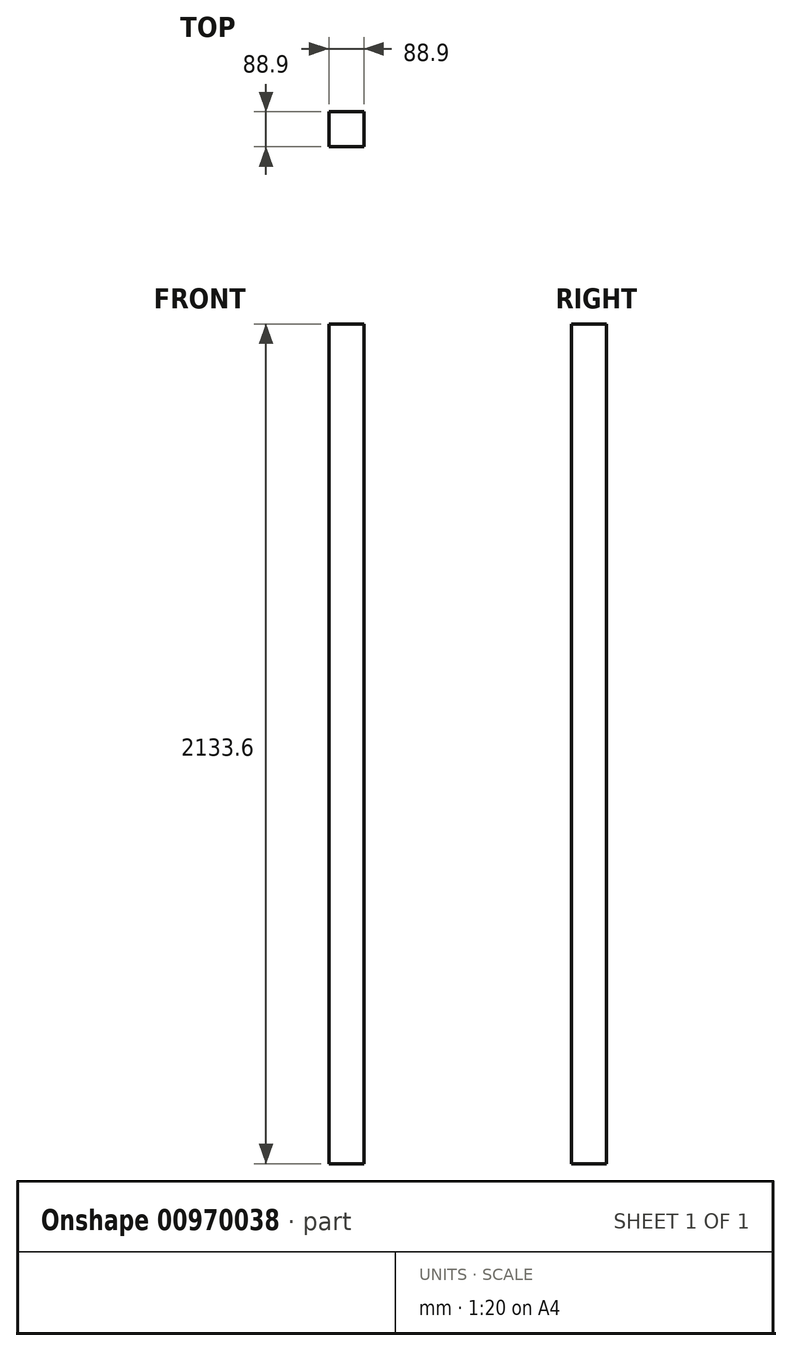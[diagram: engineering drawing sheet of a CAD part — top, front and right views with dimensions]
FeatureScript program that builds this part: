
annotation { "Feature Type Name" : "Feature", "Feature Type Description" : "" }
export const myFeature = defineFeature(function(context is Context, id is Id, definition is map)
    precondition{}
    {
        {
            var Q0;
            Q0=qCreatedBy(makeId("Front.planeOp"),FACE);
            var sketch = newSketch(context, id + "F0", { "sketchPlane" : qUnion([Q0])});
            skLineSegment(sketch, "E0.bottom", {"start": v(0, 0) * mm, "end": v(88.9, 0) * mm});
            skLineSegment(sketch, "E0.top", {"start": v(0, 2133.6) * mm, "end": v(88.9, 2133.6) * mm});
            skLineSegment(sketch, "E0.left", {"start": v(0, 0) * mm, "end": v(0, 2133.6) * mm});
            skLineSegment(sketch, "E0.right", {"start": v(88.9, 0) * mm, "end": v(88.9, 2133.6) * mm});
            skSolve(sketch);
        }
        {
            var Q0;
            Q0=makeQuery(id+"F0.imprint","IMPRINT",FACE,{"disambiguationData":[TD([[makeQuery(id+"F0.imprint","IMPRINT",EDGE,{"derivedFrom":sQuery(id+"F0.wireOp",EDGE,"E0.bottom")}),1.0]])]});
            extrude(context, id + "F1", {"entities" : qUnion([Q0]), "endBound" : BoundingType.SYMMETRIC, "depth" : 88.9 * mm, "offsetDistance" : 25.4 * mm});
        }
    });
